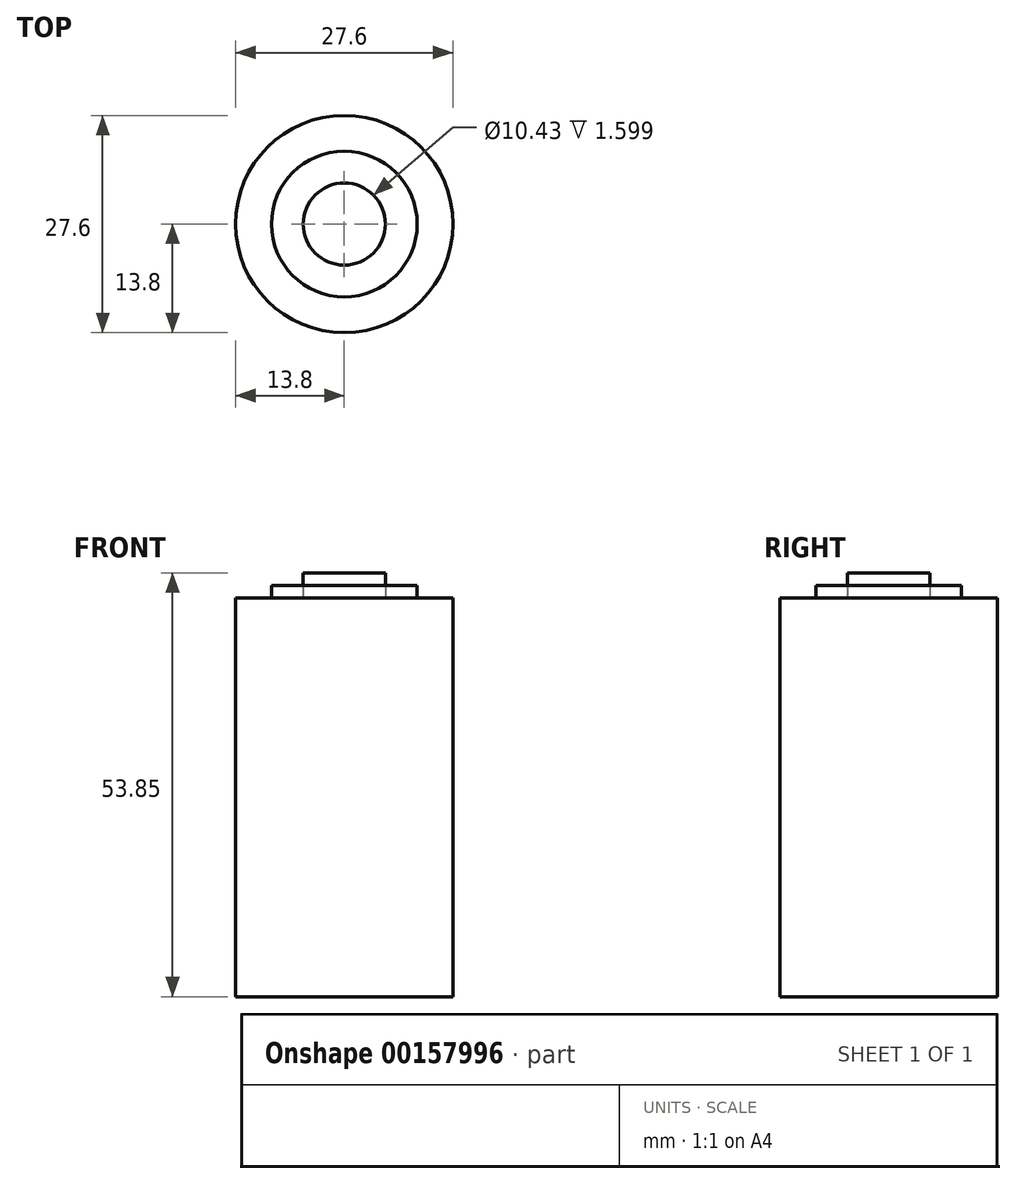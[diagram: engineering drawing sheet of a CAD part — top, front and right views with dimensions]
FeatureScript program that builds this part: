
annotation { "Feature Type Name" : "Feature", "Feature Type Description" : "" }
export const myFeature = defineFeature(function(context is Context, id is Id, definition is map)
    precondition{}
    {
        {
            var Q0;
            Q0=qCreatedBy(makeId("Front.planeOp"),FACE);
            var sketch = newSketch(context, id + "F0", { "sketchPlane" : qUnion([Q0])});
            skLineSegment(sketch, "E0.bottom", {"start": v(0, 0) * mm, "end": v(13.8, 0) * mm});
            skLineSegment(sketch, "E0.top", {"start": v(0, 50.65) * mm, "end": v(13.8, 50.65) * mm});
            skLineSegment(sketch, "E0.left", {"start": v(0, 0) * mm, "end": v(0, 50.65) * mm});
            skLineSegment(sketch, "E0.right", {"start": v(13.8, 0) * mm, "end": v(13.8, 50.65) * mm});
            skLineSegment(sketch, "E1.bottom", {"start": v(5.22, 50.65) * mm, "end": v(0, 50.65) * mm});
            skLineSegment(sketch, "E1.top", {"start": v(5.22, 53.85) * mm, "end": v(0, 53.85) * mm});
            skLineSegment(sketch, "E1.left", {"start": v(5.22, 50.65) * mm, "end": v(5.22, 53.85) * mm});
            skLineSegment(sketch, "E1.right", {"start": v(0, 50.65) * mm, "end": v(0, 53.85) * mm});
            skLineSegment(sketch, "E2.bottom", {"start": v(9.25, 50.65) * mm, "end": v(0, 50.65) * mm});
            skLineSegment(sketch, "E2.top", {"start": v(9.25, 52.25) * mm, "end": v(0, 52.25) * mm});
            skLineSegment(sketch, "E2.left", {"start": v(9.25, 50.65) * mm, "end": v(9.25, 52.25) * mm});
            skLineSegment(sketch, "E2.right", {"start": v(0, 50.65) * mm, "end": v(0, 52.25) * mm});
            skSolve(sketch);
        }
        {
            var Q0;
            {var subQ0=sQuery(id+"F0.wireOp",EDGE,"E1.top");Q0=makeQuery(id+"F0.imprint","IMPRINT",FACE,{"disambiguationData":[TD([[makeQuery(id+"F0.imprint","IMPRINT",EDGE,{"derivedFrom":subQ0}),1.0]])]});}
            var Q1;
            Q1=makeQuery(id+"F0.imprint","IMPRINT",FACE,{"disambiguationData":[TD([[makeQuery(id+"F0.imprint","IMPRINT",EDGE,{"derivedFrom":sQuery(id+"F0.wireOp",EDGE,"E0.bottom")}),1.0]])]});
            var Q2;
            {var subQ5=sQuery(id+"F0.wireOp",EDGE,"E2.left");Q2=makeQuery(id+"F0.imprint","IMPRINT",FACE,{"disambiguationData":[TD([[makeQuery(id+"F0.imprint","IMPRINT",EDGE,{"derivedFrom":subQ5}),1.0]])]});}
            var Q3;
            {var subQ5=sQuery(id+"F0.wireOp",EDGE,"E2.right");Q3=makeQuery(id+"F0.imprint","IMPRINT",FACE,{"disambiguationData":[TD([[makeQuery(id+"F0.imprint","IMPRINT",EDGE,{"derivedFrom":subQ5}),-1.0]])]});}
            var Q4;
            Q4=sQuery(id+"F0.wireOp",EDGE,"E0.left");
            revolve(context, id + "F1", {"entities" : qUnion([Q0, Q1, Q2, Q3]), "axis" : qUnion([Q4]), "revolveType" : RevolveType.FULL});
        }
    });
